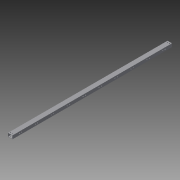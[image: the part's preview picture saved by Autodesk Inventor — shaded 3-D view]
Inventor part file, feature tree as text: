
AUTODESK INVENTOR PART (.ipt)
format: ipt  version: 2015 SP1 (Build 190203100, 203)  size: 155,648 bytes
history: native  units: in
note: dims shown in document units (in); Inventor stores cm internally (conversion verified against a paired STEP export)
features: extrude x3, sketch x2
ambient origin geometry x8: Origin, YZ Plane, XZ Plane, XY Plane, X Axis, Y Axis, Z Axis, Center Point
bodies: Solid1 (feature_tree)
feature tree (5):
  extrude  "Extrusion1"  Depth=1.1811in
  extrude  "Extrusion2"  Depth=56.2992in TaperAngle=0.0deg
  extrude  "Extrusion3"  Depth=0.0787in
  sketch  "Sketch3"  dims[d0=1.5748in d1=1.1811in]
  sketch  "Sketch4"  dims[d3=0.0787in d4=56.2992in d5=0.0in d6=0.0787in d7=0.0787in d8=0.0787in d14=3.937in d16=5.6299in d17=0.3937in d19=0.3937in d21=0.3937in d22=0.0in d23=0.2756in d24=0.4921in d25=0.7087in d26=0.4921in d27=0.0in d28=0.0in d47=3.937in d49=5.6299in d50=0.3937in d52=0.3937in d54=2.815in d55=0.7874in d56=0.2756in d57=0.2756in d58=3.937in d60=5.6299in d61=0.3937in d63=0.3937in]
